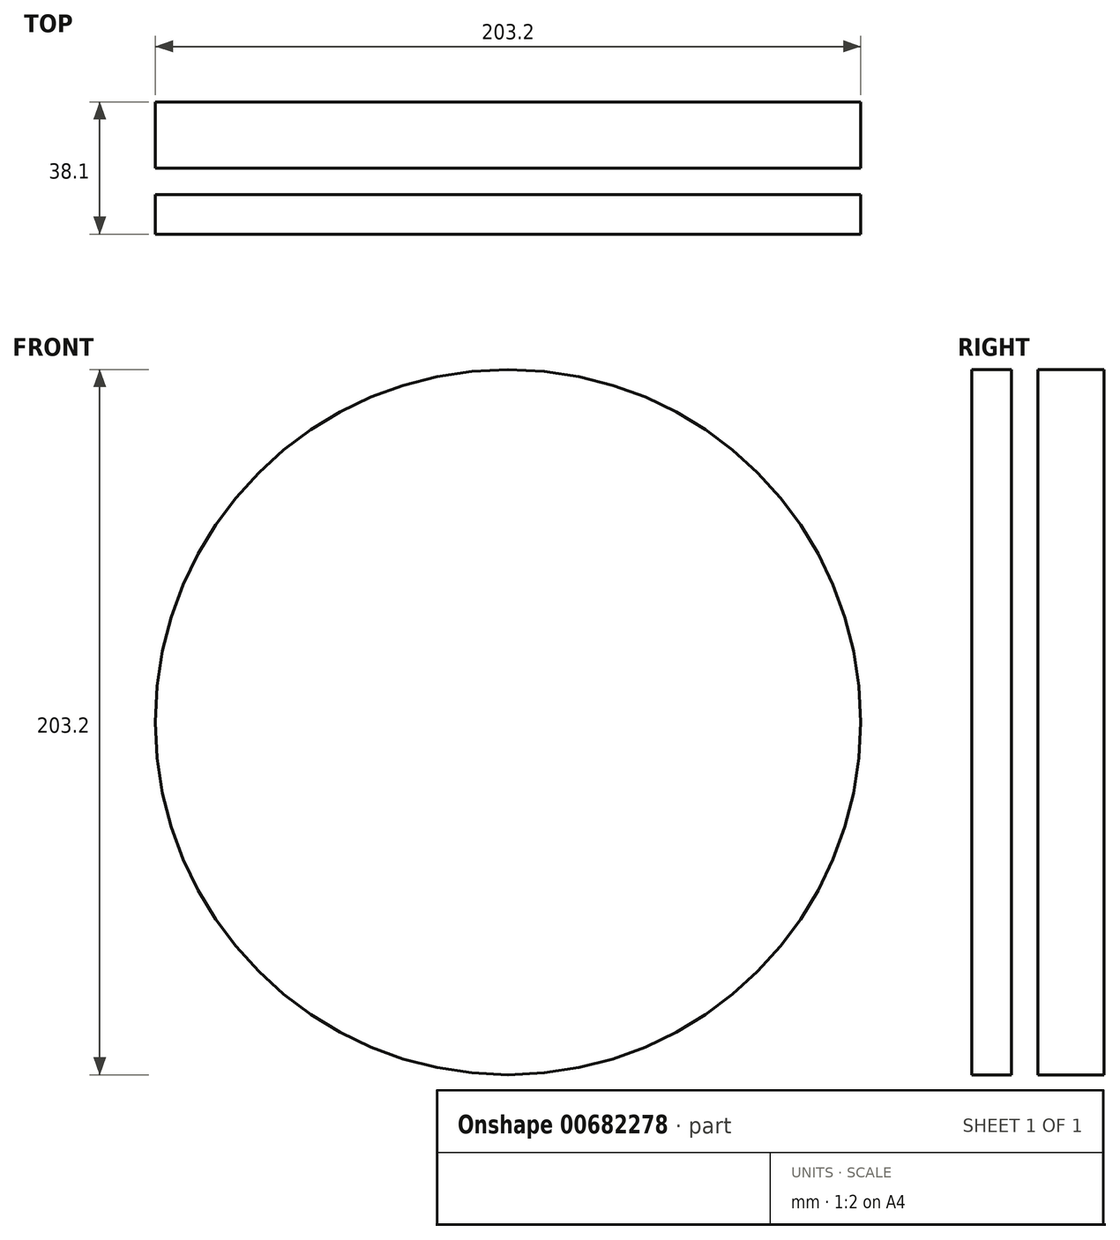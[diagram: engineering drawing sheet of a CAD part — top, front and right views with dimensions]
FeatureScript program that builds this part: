
annotation { "Feature Type Name" : "Feature", "Feature Type Description" : "" }
export const myFeature = defineFeature(function(context is Context, id is Id, definition is map)
    precondition{}
    {
        {
            var Q0;
            Q0=qCreatedBy(makeId("Front.planeOp"),FACE);
            var sketch = newSketch(context, id + "F0", { "sketchPlane" : qUnion([Q0])});
            skCircle(sketch, "E0", {"center": v(0, 0) * mm, "radius": 101.6 * mm});
            skSolve(sketch);
        }
        {
            var Q0;
            Q0 = qSketchRegion(id + "F0", true);
            extrude(context, id + "F1", {"entities" : qUnion([Q0]), "depth" : 38.1 * mm, "offsetDistance" : 25.4 * mm, "symmetric" : true});
        }
        {
            var Q0;
            Q0=qCreatedBy(makeId("Front.planeOp"),FACE);
            var sketch = newSketch(context, id + "F2", { "sketchPlane" : qUnion([Q0])});
            skCircle(sketch, "E1", {"center": v(0, 0) * mm, "radius": 101.6 * mm});
            skSolve(sketch);
        }
        {
            var Q0;
            Q0 = qSketchRegion(id + "F2", true);
            extrude(context, id + "F3", {"entities" : qUnion([Q0]), "operationType" : NewBodyOperationType.REMOVE, "depth" : 7.62 * mm, "offsetDistance" : 25.4 * mm});
        }
    });
